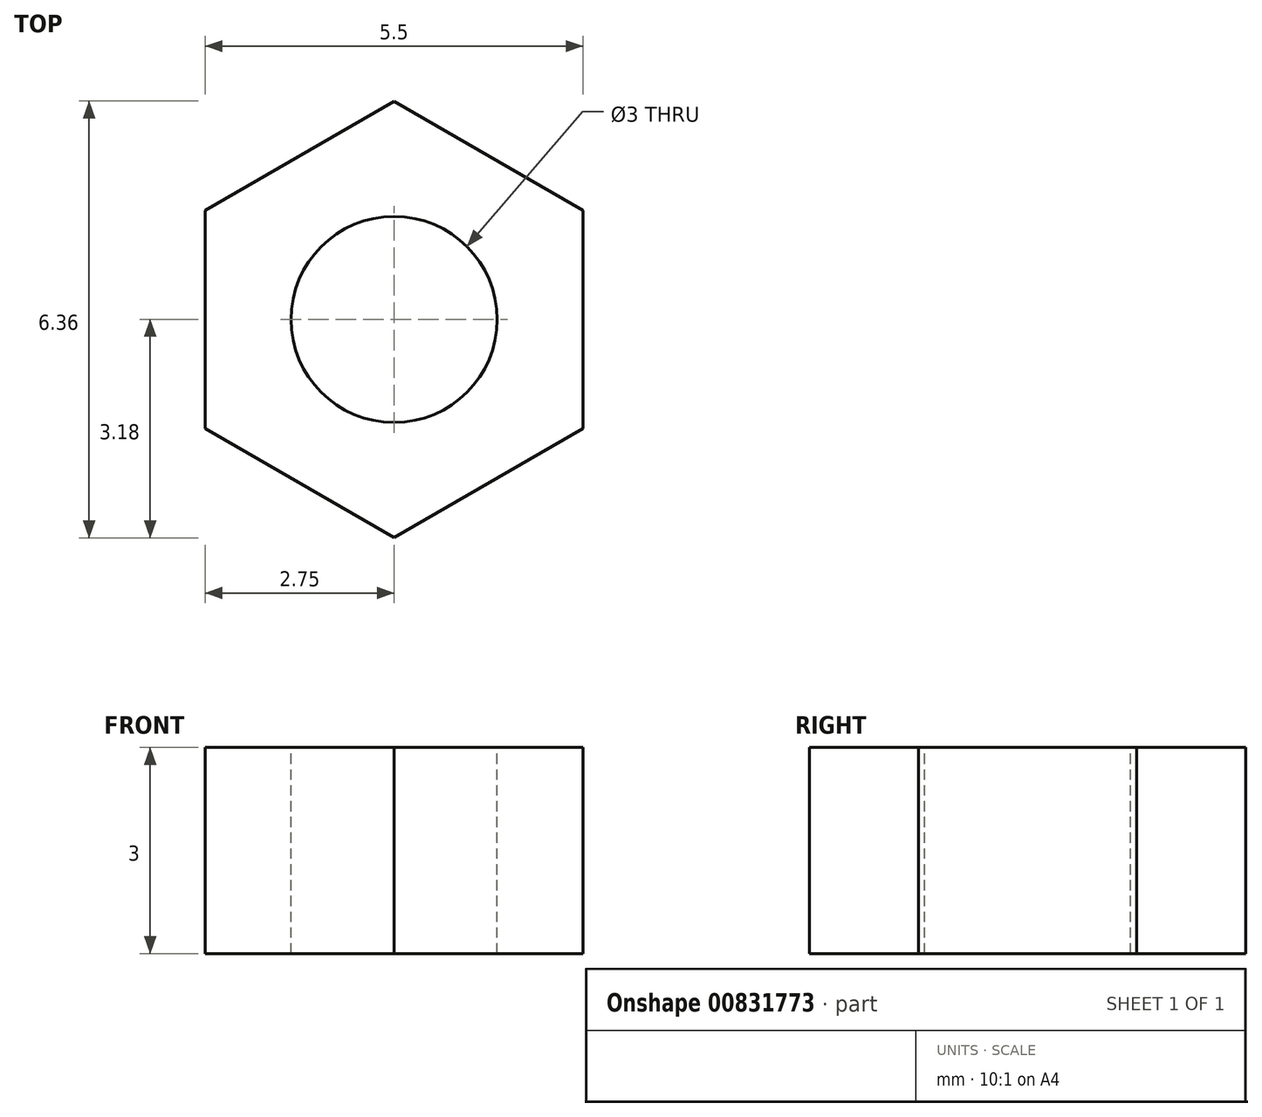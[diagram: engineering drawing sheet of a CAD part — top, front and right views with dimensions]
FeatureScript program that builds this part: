
annotation { "Feature Type Name" : "Feature", "Feature Type Description" : "" }
export const myFeature = defineFeature(function(context is Context, id is Id, definition is map)
    precondition{}
    {
        {
            var Q0;
            Q0=qCreatedBy(makeId("Top.planeOp"),FACE);
            var sketch = newSketch(context, id + "F0", { "sketchPlane" : qUnion([Q0])});
            skLineSegment(sketch, "E0", {"start": v(-2.75, 1.59) * mm, "end": v(0, 3.18) * mm});
            skLineSegment(sketch, "E1", {"start": v(2.75, 1.59) * mm, "end": v(0, 3.18) * mm});
            skLineSegment(sketch, "E2", {"start": v(2.75, 1.59) * mm, "end": v(2.75, -1.59) * mm});
            skLineSegment(sketch, "E3", {"start": v(2.75, -1.59) * mm, "end": v(0, -3.18) * mm});
            skLineSegment(sketch, "E4", {"start": v(0, -3.18) * mm, "end": v(-2.75, -1.59) * mm});
            skLineSegment(sketch, "E5", {"start": v(-2.75, -1.59) * mm, "end": v(-2.75, 1.59) * mm});
            skPoint(sketch, "E6.center.orphan", {"position": v(0, 0) * mm});
            skSolve(sketch);
        }
        {
            var Q0;
            Q0=makeQuery(id+"F0.imprint","IMPRINT",FACE,{"disambiguationData":[TD([[makeQuery(id+"F0.imprint","IMPRINT",EDGE,{"derivedFrom":sQuery(id+"F0.wireOp",EDGE,"E0")}),-1.0]])]});
            extrude(context, id + "F1", {"entities" : qUnion([Q0]), "depth" : 3 * mm, "offsetDistance" : 25 * mm});
        }
        {
            var Q0;
            Q0=makeQuery(id+"F1.opExtrude","CAP_FACE",FACE,{"disambiguationData":[OSD([sQuery(id+"F0.wireOp",EDGE,"E0"),sQuery(id+"F0.wireOp",EDGE,"E1"),sQuery(id+"F0.wireOp",EDGE,"E2"),sQuery(id+"F0.wireOp",EDGE,"E3"),sQuery(id+"F0.wireOp",EDGE,"E4"),sQuery(id+"F0.wireOp",EDGE,"E5")])],"isStart":false});
            var sketch = newSketch(context, id + "F2", { "sketchPlane" : qUnion([Q0])});
            skCircle(sketch, "E7", {"center": v(0, 0) * mm, "radius": 1.5 * mm});
            skSolve(sketch);
        }
        {
            var Q0;
            Q0=makeQuery(id+"F2.imprint","IMPRINT",FACE,{"disambiguationData":[TD([[makeQuery(id+"F2.imprint","IMPRINT",EDGE,{"derivedFrom":sQuery(id+"F2.wireOp",EDGE,"E7")}),1.0]])]});
            extrude(context, id + "F3", {"entities" : qUnion([Q0]), "operationType" : NewBodyOperationType.REMOVE, "endBound" : BoundingType.THROUGH_ALL, "oppositeDirection" : true, "depth" : 25 * mm, "offsetDistance" : 25 * mm});
        }
    });
